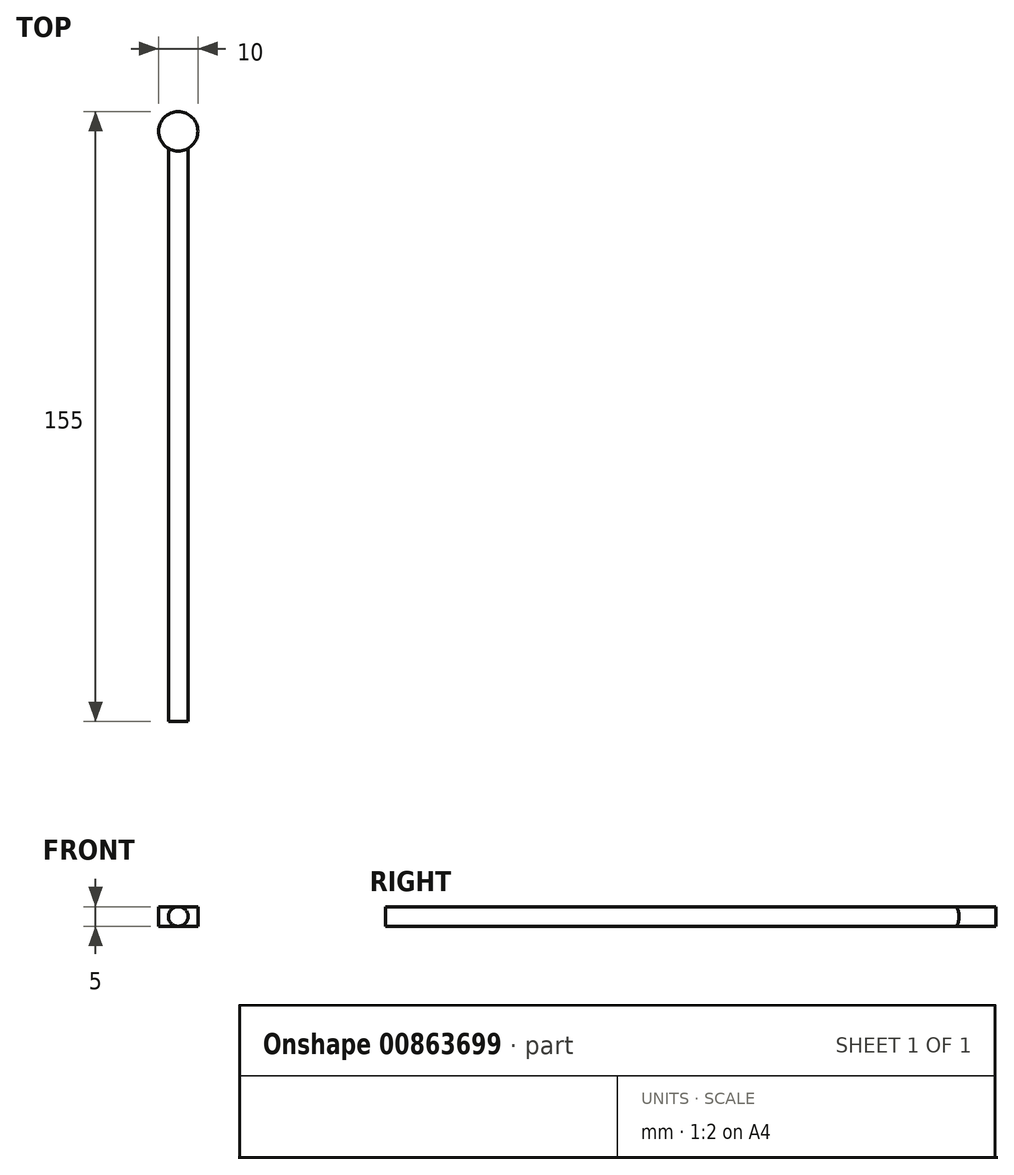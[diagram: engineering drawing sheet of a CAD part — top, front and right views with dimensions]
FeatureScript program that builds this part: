
annotation { "Feature Type Name" : "Feature", "Feature Type Description" : "" }
export const myFeature = defineFeature(function(context is Context, id is Id, definition is map)
    precondition{}
    {
        {
            var Q0;
            Q0=qCreatedBy(makeId("Front.planeOp"),FACE);
            var sketch = newSketch(context, id + "F0", { "sketchPlane" : qUnion([Q0])});
            skCircle(sketch, "E0", {"center": v(0, 0) * mm, "radius": 2.5 * mm});
            skSolve(sketch);
        }
        {
            var Q0;
            Q0=makeQuery(id+"F0.imprint","IMPRINT",FACE,{"disambiguationData":[TD([[makeQuery(id+"F0.imprint","IMPRINT",EDGE,{"derivedFrom":sQuery(id+"F0.wireOp",EDGE,"E0")}),1.0]])]});
            extrude(context, id + "F1", {"entities" : qUnion([Q0]), "depth" : 150 * mm, "offsetDistance" : 25 * mm});
        }
        {
            var Q0;
            Q0=qCreatedBy(makeId("Top.planeOp"),FACE);
            var sketch = newSketch(context, id + "F2", { "sketchPlane" : qUnion([Q0])});
            skCircle(sketch, "E1", {"center": v(0, 0) * mm, "radius": 5 * mm});
            skSolve(sketch);
        }
        {
            var Q0;
            Q0=makeQuery(id+"F2.imprint","IMPRINT",FACE,{"disambiguationData":[TD([[makeQuery(id+"F2.imprint","IMPRINT",EDGE,{"derivedFrom":sQuery(id+"F2.wireOp",EDGE,"E1")}),1.0]])]});
            extrude(context, id + "F3", {"entities" : qUnion([Q0]), "operationType" : NewBodyOperationType.ADD, "endBound" : BoundingType.SYMMETRIC, "depth" : 5 * mm, "offsetDistance" : 25 * mm});
        }
    });
